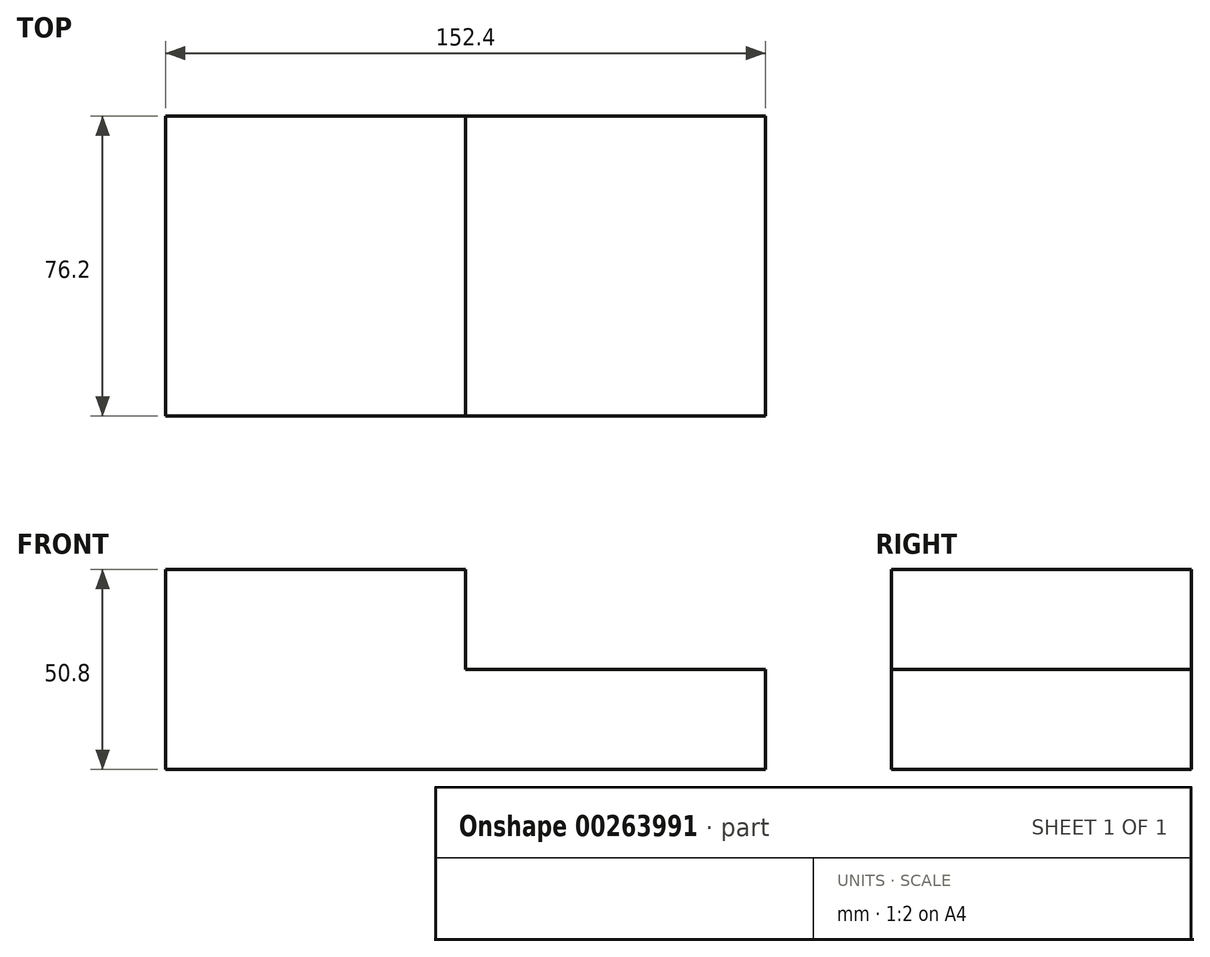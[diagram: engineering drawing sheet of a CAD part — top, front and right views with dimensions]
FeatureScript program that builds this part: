
annotation { "Feature Type Name" : "Feature", "Feature Type Description" : "" }
export const myFeature = defineFeature(function(context is Context, id is Id, definition is map)
    precondition{}
    {
        {
            var Q0;
            Q0=qCreatedBy(makeId("Front.planeOp"),FACE);
            var sketch = newSketch(context, id + "F0", { "sketchPlane" : qUnion([Q0])});
            skLineSegment(sketch, "E0", {"start": v(0, 0) * mm, "end": v(-76.2, 0) * mm});
            skLineSegment(sketch, "E1", {"start": v(0, 0) * mm, "end": v(76.2, 0) * mm});
            skLineSegment(sketch, "E2", {"start": v(-76.2, 0) * mm, "end": v(-76.2, 50.8) * mm});
            skLineSegment(sketch, "E3", {"start": v(-76.2, 50.8) * mm, "end": v(0, 50.8) * mm});
            skLineSegment(sketch, "E4", {"start": v(0, 50.8) * mm, "end": v(0, 25.4) * mm});
            skLineSegment(sketch, "E5", {"start": v(0, 25.4) * mm, "end": v(76.2, 25.4) * mm});
            skLineSegment(sketch, "E6", {"start": v(76.2, 25.4) * mm, "end": v(76.2, 0) * mm});
            skSolve(sketch);
        }
        {
            var Q0;
            Q0=makeQuery(id+"F0.imprint","IMPRINT",FACE,{"disambiguationData":[TD([[makeQuery(id+"F0.imprint","IMPRINT",EDGE,{"derivedFrom":sQuery(id+"F0.wireOp",EDGE,"E0")}),-1.0]])]});
            extrude(context, id + "F1", {"entities" : qUnion([Q0]), "depth" : 76.2 * mm});
        }
    });
